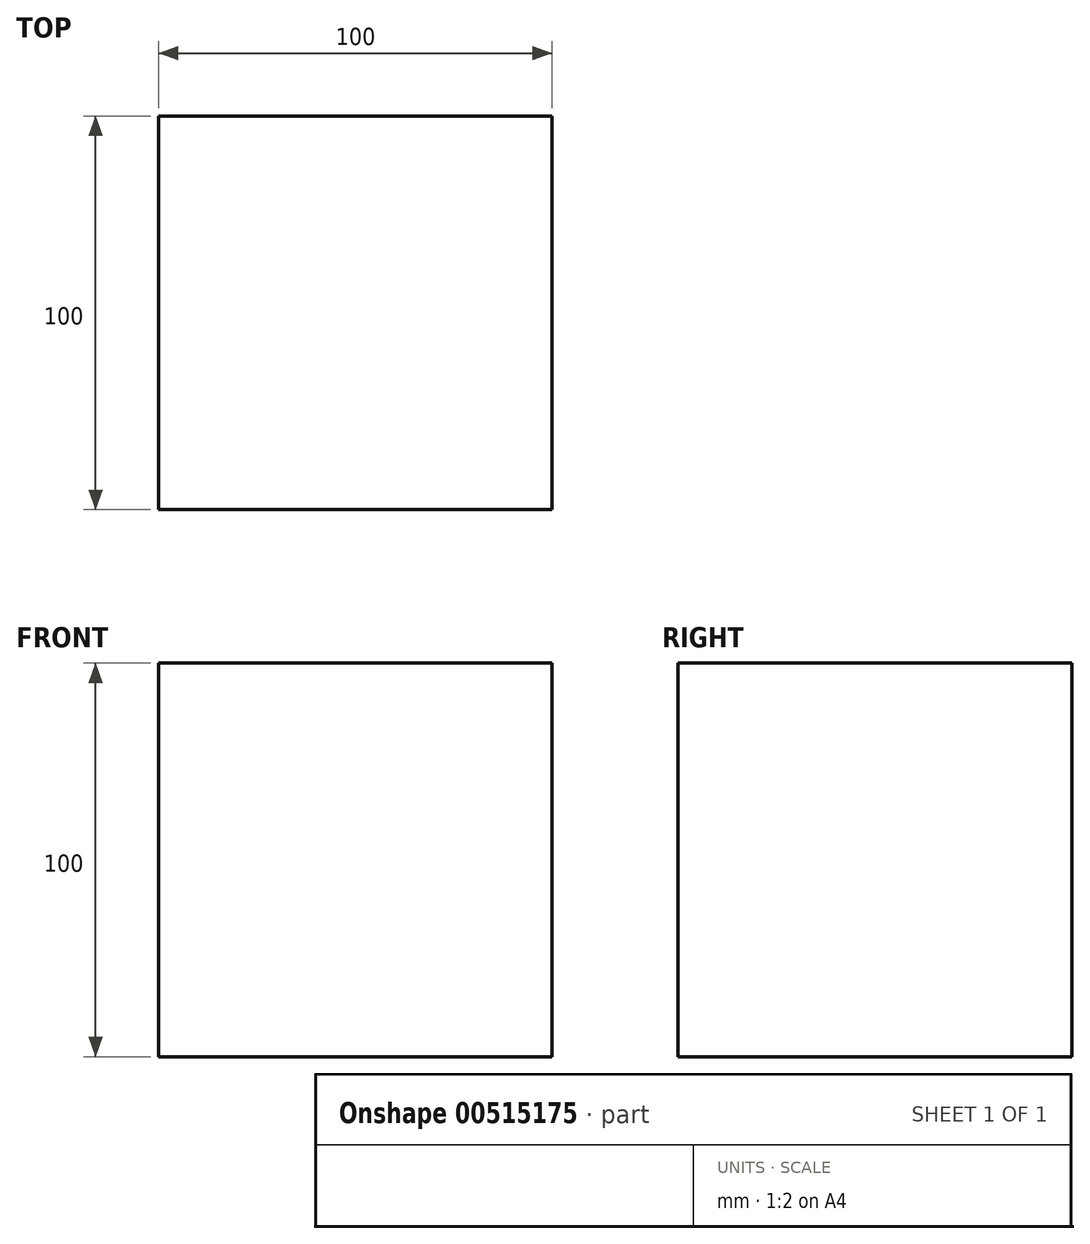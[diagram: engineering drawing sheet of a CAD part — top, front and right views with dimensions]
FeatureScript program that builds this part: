
annotation { "Feature Type Name" : "Feature", "Feature Type Description" : "" }
export const myFeature = defineFeature(function(context is Context, id is Id, definition is map)
    precondition{}
    {
        {
            var Q0;
            Q0=qCreatedBy(makeId("Front.planeOp"),FACE);
            var sketch = newSketch(context, id + "F0", { "sketchPlane" : qUnion([Q0])});
            skLineSegment(sketch, "E0.bottom", {"start": v(50, 50) * mm, "end": v(-50, 50) * mm});
            skLineSegment(sketch, "E0.top", {"start": v(50, -50) * mm, "end": v(-50, -50) * mm});
            skLineSegment(sketch, "E0.left", {"start": v(50, 50) * mm, "end": v(50, -50) * mm});
            skLineSegment(sketch, "E0.right", {"start": v(-50, 50) * mm, "end": v(-50, -50) * mm});
            skPoint(sketch, "E0.middle", {"position": v(0, 0) * mm});
            skSolve(sketch);
        }
        {
            var Q0;
            Q0 = qSketchRegion(id + "F0", true);
            extrude(context, id + "F1", {"entities" : qUnion([Q0]), "depth" : 100 * mm, "offsetDistance" : 25 * mm});
        }
    });
